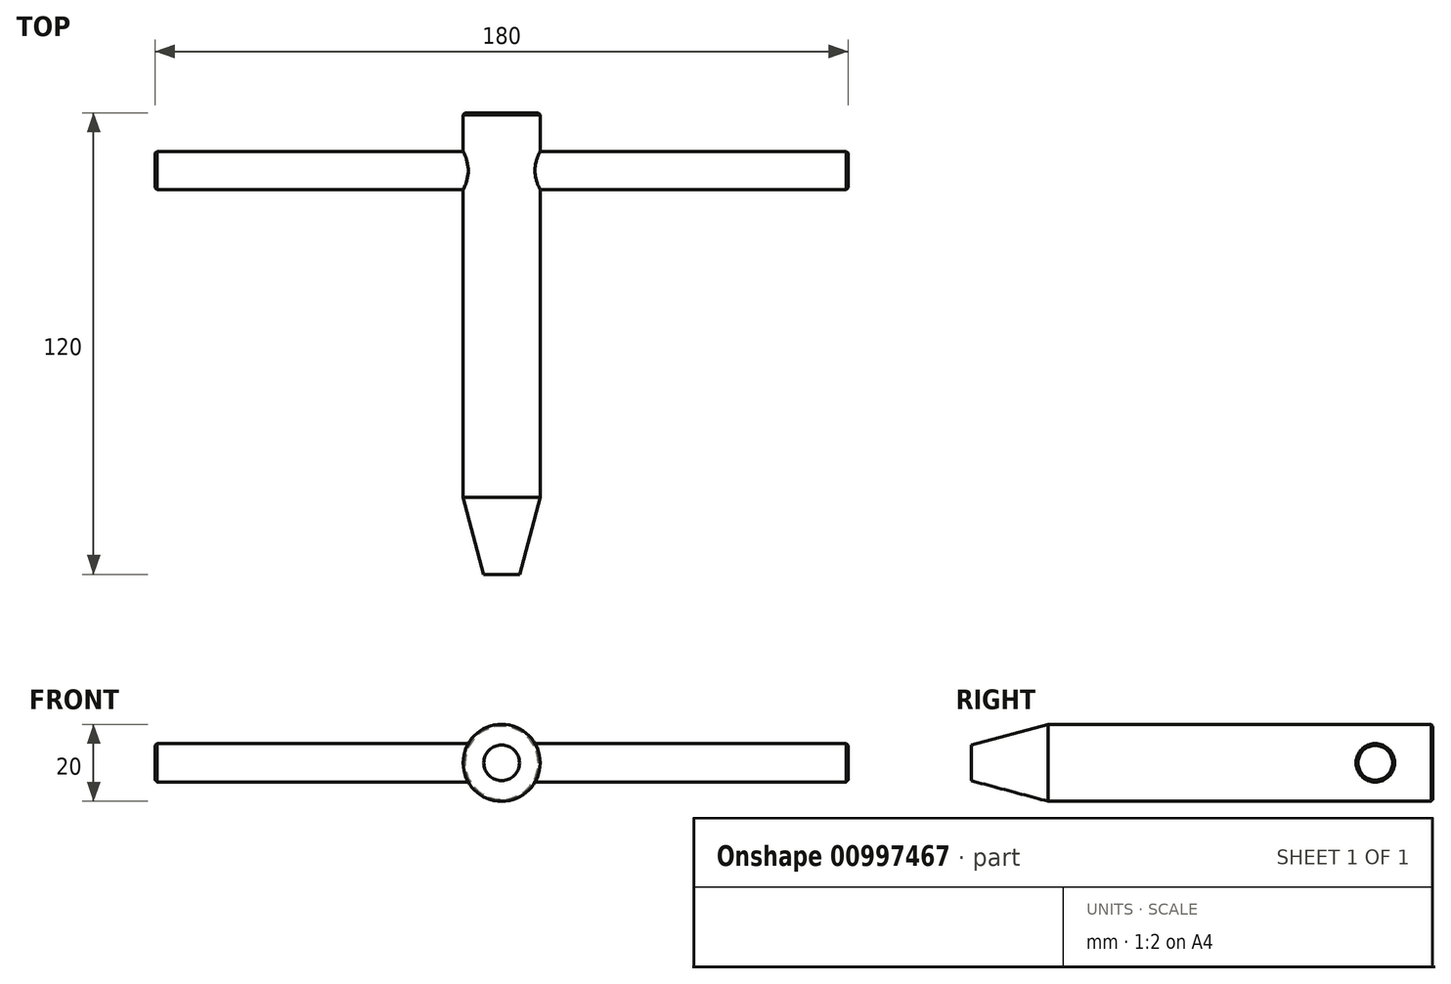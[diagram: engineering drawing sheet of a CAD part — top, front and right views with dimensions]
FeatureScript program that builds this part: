
annotation { "Feature Type Name" : "Feature", "Feature Type Description" : "" }
export const myFeature = defineFeature(function(context is Context, id is Id, definition is map)
    precondition{}
    {
        {
            var Q0;
            Q0=qCreatedBy(makeId("Front.planeOp"),FACE);
            var sketch = newSketch(context, id + "F0", { "sketchPlane" : qUnion([Q0])});
            skCircle(sketch, "E0", {"center": v(0, 0) * mm, "radius": 10 * mm});
            skSolve(sketch);
        }
        {
            var Q0;
            Q0=makeQuery(id+"F0.imprint","IMPRINT",FACE,{"disambiguationData":[TD([[makeQuery(id+"F0.imprint","IMPRINT",EDGE,{"derivedFrom":sQuery(id+"F0.wireOp",EDGE,"E0")}),1.0]])]});
            extrude(context, id + "F1", {"entities" : qUnion([Q0]), "depth" : 100 * mm, "offsetDistance" : 25 * mm});
        }
        {
            var Q0;
            Q0=makeQuery(id+"F1.opExtrude","CAP_FACE",FACE,{"disambiguationData":[OSD([sQuery(id+"F0.wireOp",EDGE,"E0")])],"isStart":false});
            var sketch = newSketch(context, id + "F2", { "sketchPlane" : qUnion([Q0])});
            skCircle(sketch, "E1", {"center": v(0, 0) * mm, "radius": 10 * mm});
            skSolve(sketch);
        }
        {
            var Q0;
            Q0=makeQuery(id+"F2.imprint","IMPRINT",FACE,{"disambiguationData":[TD([[makeQuery(id+"F2.imprint","IMPRINT",EDGE,{"derivedFrom":sQuery(id+"F2.wireOp",EDGE,"E1")}),1.0]])]});
            extrude(context, id + "F3", {"entities" : qUnion([Q0]), "operationType" : NewBodyOperationType.ADD, "depth" : 20 * mm, "offsetDistance" : 25 * mm, "hasDraft" : true, "draftAngle" : 15 * degree, "draftPullDirection" : true});
        }
        {
            var Q0;
            Q0=qCreatedBy(makeId("Right.planeOp"),FACE);
            cPlane(context, id + "F4", {"entities" : qUnion([Q0]), "cplaneType" : CPlaneType.OFFSET, "offset" : 10 * mm, "width" : 150 * mm, "height" : 150 * mm});
        }
        {
            var Q0;
            Q0=qCreatedBy(id+"F4.planeOp",FACE);
            var sketch = newSketch(context, id + "F5", { "sketchPlane" : qUnion([Q0])});
            skCircle(sketch, "E2", {"center": v(-15, 0) * mm, "radius": 5 * mm});
            skSolve(sketch);
        }
        {
            var Q0;
            Q0=makeQuery(id+"F5.imprint","IMPRINT",FACE,{"disambiguationData":[TD([[makeQuery(id+"F5.imprint","IMPRINT",EDGE,{"derivedFrom":sQuery(id+"F5.wireOp",EDGE,"E2")}),1.0]])]});
            extrude(context, id + "F6", {"entities" : qUnion([Q0]), "operationType" : NewBodyOperationType.ADD, "depth" : 80 * mm, "offsetDistance" : 25 * mm, "hasSecondDirection" : true, "secondDirectionOppositeDirection" : true, "secondDirectionDepth" : 3 * mm});
        }
        {
            var Q0;
            Q0=qCreatedBy(makeId("Right.planeOp"),FACE);
            cPlane(context, id + "F7", {"entities" : qUnion([Q0]), "cplaneType" : CPlaneType.OFFSET, "offset" : 10 * mm, "oppositeDirection" : true, "width" : 150 * mm, "height" : 150 * mm});
        }
        {
            var Q0;
            Q0=qCreatedBy(id+"F7.planeOp",FACE);
            var sketch = newSketch(context, id + "F8", { "sketchPlane" : qUnion([Q0])});
            skCircle(sketch, "E3", {"center": v(-15, 0) * mm, "radius": 5 * mm});
            skSolve(sketch);
        }
        {
            var Q0;
            Q0=makeQuery(id+"F8.imprint","IMPRINT",FACE,{"disambiguationData":[TD([[makeQuery(id+"F8.imprint","IMPRINT",EDGE,{"derivedFrom":sQuery(id+"F8.wireOp",EDGE,"E3")}),1.0]])]});
            extrude(context, id + "F9", {"entities" : qUnion([Q0]), "operationType" : NewBodyOperationType.ADD, "oppositeDirection" : true, "depth" : 80 * mm, "offsetDistance" : 25 * mm, "hasSecondDirection" : true, "secondDirectionOppositeDirection" : false, "secondDirectionDepth" : 3 * mm});
        }
        {
            var Q0;
            Q0=makeQuery(id+"F9.opExtrude","CAP_EDGE",EDGE,{"disambiguationData":[OSD([sQuery(id+"F8.wireOp",EDGE,"E3")])],"isStart":false});
            var Q1;
            Q1=makeQuery(id+"F1.opExtrude","CAP_EDGE",EDGE,{"disambiguationData":[OSD([sQuery(id+"F0.wireOp",EDGE,"E0")])],"isStart":true});
            var Q2;
            Q2=makeQuery(id+"F6.opExtrude","CAP_EDGE",EDGE,{"disambiguationData":[OSD([sQuery(id+"F5.wireOp",EDGE,"E2")])],"isStart":false});
            chamfer(context, id + "F10", {"entities" : qUnion([Q0, Q1, Q2]), "width" : 0.5 * mm, "tangentPropagation" : true});
        }
    });
